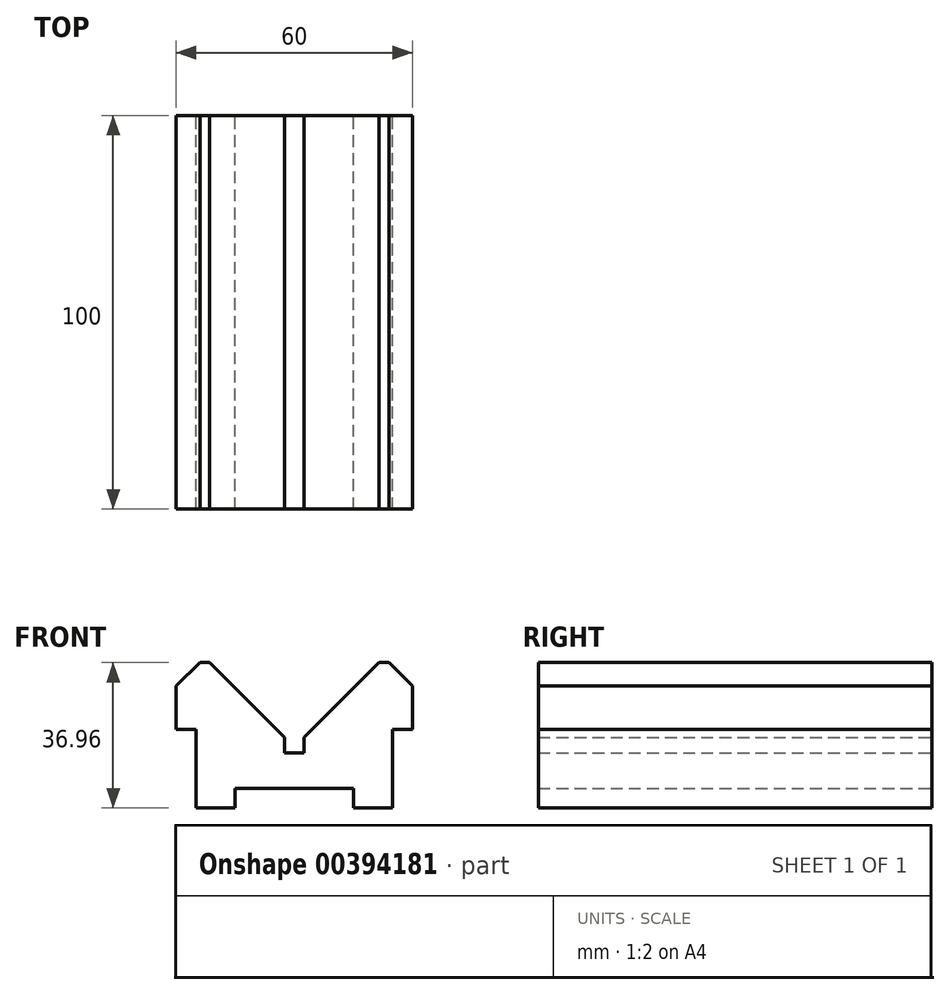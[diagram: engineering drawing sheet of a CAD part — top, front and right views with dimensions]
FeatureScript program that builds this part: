
annotation { "Feature Type Name" : "Feature", "Feature Type Description" : "" }
export const myFeature = defineFeature(function(context is Context, id is Id, definition is map)
    precondition{}
    {
        {
            var Q0;
            Q0=qCreatedBy(makeId("Front.planeOp"),FACE);
            var sketch = newSketch(context, id + "F0", { "sketchPlane" : qUnion([Q0])});
            skLineSegment(sketch, "E0.bottom", {"start": v(-24, 31.96) * mm, "end": v(-21.5, 31.96) * mm});
            skLineSegment(sketch, "E0.top", {"start": v(-25, -5) * mm, "end": v(-15, -5) * mm});
            skLineSegment(sketch, "E0.left", {"start": v(-30, 25.96) * mm, "end": v(-30, 15) * mm});
            skLineSegment(sketch, "E0.right", {"start": v(30, 25.96) * mm, "end": v(30, 15) * mm});
            skLineSegment(sketch, "E1", {"start": v(-15, 0) * mm, "end": v(15, 0) * mm});
            skLineSegment(sketch, "E2", {"start": v(-15, -5) * mm, "end": v(-15, 0) * mm});
            skLineSegment(sketch, "E3", {"start": v(15, -5) * mm, "end": v(15, 0) * mm});
            skLineSegment(sketch, "E4", {"start": v(-30, 15) * mm, "end": v(-25, 15) * mm});
            skPoint(sketch, "E5.trimOffspring.start.orphan", {"position": v(-30, 0) * mm});
            skPoint(sketch, "E6.orphan", {"position": v(-30, -5) * mm});
            skLineSegment(sketch, "E7.trimOffspring", {"start": v(15, -5) * mm, "end": v(25, -5) * mm});
            skLineSegment(sketch, "E8.trimOffspring", {"start": v(-25, 15) * mm, "end": v(-25, -5) * mm});
            skLineSegment(sketch, "E9.trimOffspring", {"start": v(25, 15) * mm, "end": v(25, -5) * mm});
            skPoint(sketch, "E10.end.orphan", {"position": v(-24, 25.96) * mm});
            skPoint(sketch, "E11.start.orphan", {"position": v(25.75, 25.96) * mm});
            skPoint(sketch, "E12.orphan", {"position": v(30, 25.96) * mm});
            skLineSegment(sketch, "E13", {"start": v(-30, 25.96) * mm, "end": v(-24, 31.96) * mm});
            skLineSegment(sketch, "E14", {"start": v(30, 25.96) * mm, "end": v(24, 31.96) * mm});
            skLineSegment(sketch, "E15", {"start": v(-2.5, 8.96) * mm, "end": v(2.5, 8.96) * mm});
            skLineSegment(sketch, "E16.trimOffspring", {"start": v(25, 15) * mm, "end": v(30, 15) * mm});
            skPoint(sketch, "E17.end.orphan", {"position": v(2.5, 31.96) * mm});
            skLineSegment(sketch, "E18.trimOffspring", {"start": v(21.5, 31.96) * mm, "end": v(24, 31.96) * mm});
            skLineSegment(sketch, "E19", {"start": v(2.5, 12.96) * mm, "end": v(2.5, 8.96) * mm});
            skLineSegment(sketch, "E20", {"start": v(-2.5, 12.96) * mm, "end": v(-2.5, 8.96) * mm});
            skLineSegment(sketch, "E21", {"start": v(21.5, 31.96) * mm, "end": v(2.5, 12.96) * mm});
            skLineSegment(sketch, "E22", {"start": v(-21.5, 31.96) * mm, "end": v(-2.5, 12.96) * mm});
            skPoint(sketch, "E23.end.orphan", {"position": v(-21.5, 25.96) * mm});
            skPoint(sketch, "E24.trimOffspring.start.orphan", {"position": v(21.5, 25.96) * mm});
            skSolve(sketch);
        }
        {
            var Q0;
            Q0=qSketchRegion(id+"F0",true);
            extrude(context, id + "F1", {"entities" : qUnion([Q0]), "depth" : 100 * mm});
        }
    });
